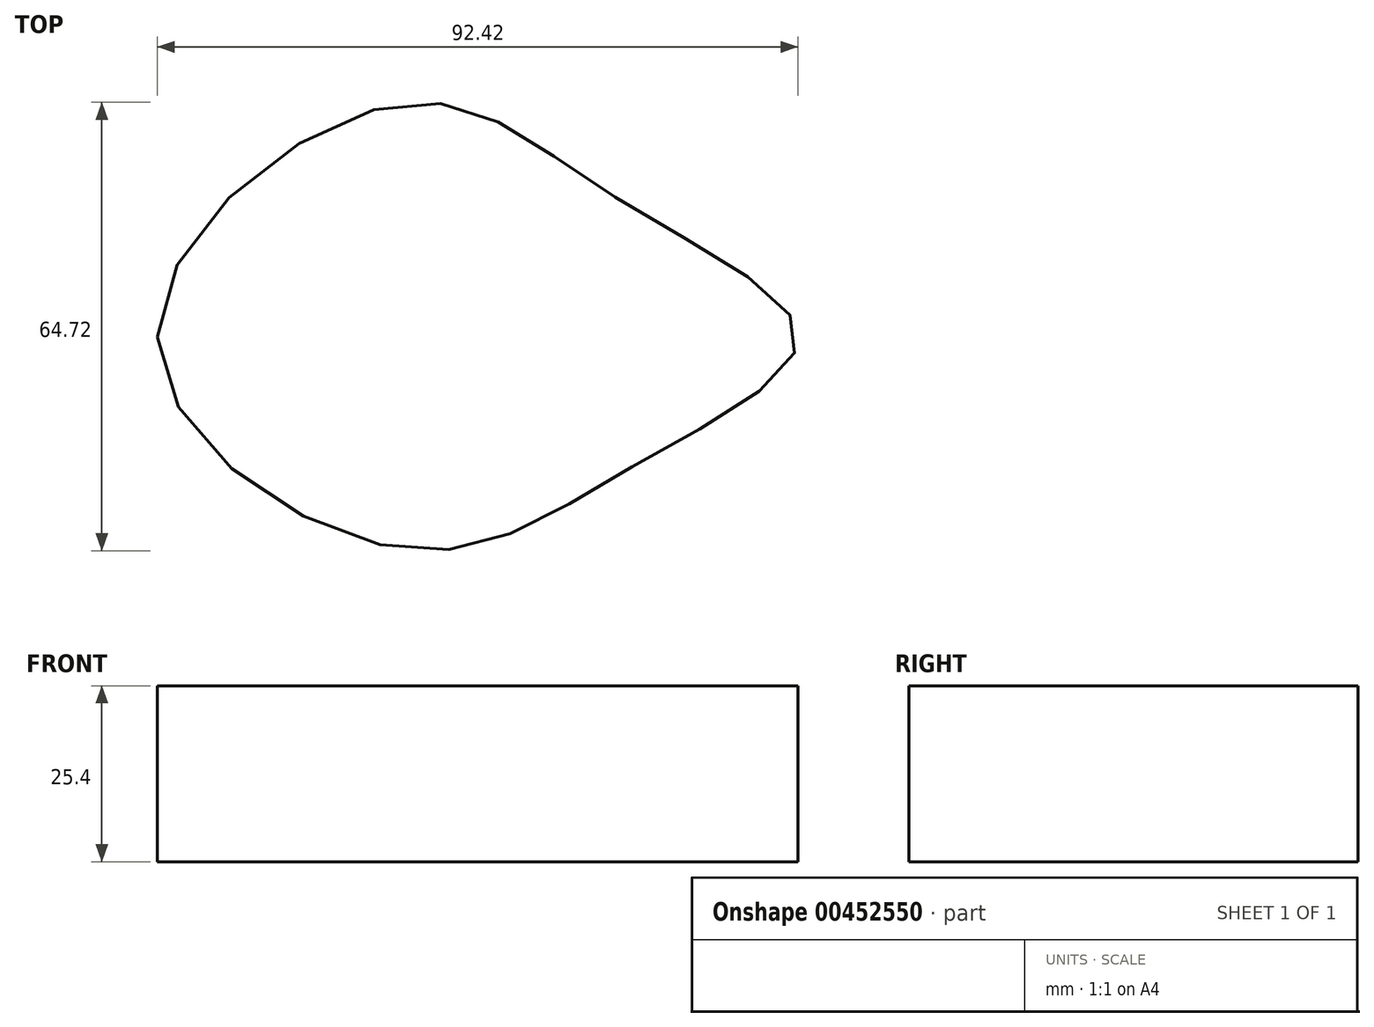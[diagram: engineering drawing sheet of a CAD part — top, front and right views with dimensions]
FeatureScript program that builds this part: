
annotation { "Feature Type Name" : "Feature", "Feature Type Description" : "" }
export const myFeature = defineFeature(function(context is Context, id is Id, definition is map)
    precondition{}
    {
        {
            var Q0;
            Q0=qCreatedBy(makeId("Top.planeOp"),FACE);
            var sketch = newSketch(context, id + "F0", { "sketchPlane" : qUnion([Q0])});
            skFitSpline(sketch, "E0", {"points": [v(-34.67, 0) * mm, v(0, 33.6) * mm, v(30.93, 20.47) * mm, v(57.75, 0) * mm, v(33.22, -19.08) * mm, v(0, -30.5) * mm, v(-34.67, 0) * mm]});
            skSolve(sketch);
        }
        {
            var Q0;
            Q0=sQuery(id+"F0.wireOp",EDGE,"E0");
            extrude(context, id + "F1", {"bodyType" : ToolBodyType.SURFACE, "surfaceEntities" : qUnion([Q0]), "depth" : 25.4 * mm});
        }
    });
